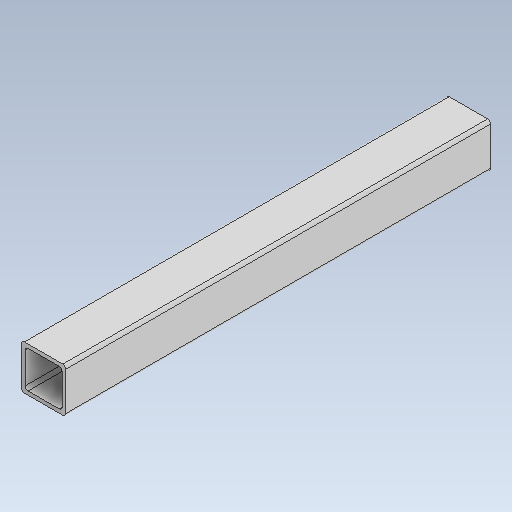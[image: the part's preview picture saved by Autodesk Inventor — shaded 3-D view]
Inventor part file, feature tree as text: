
AUTODESK INVENTOR PART (.ipt)
format: ipt  version: 2021 (Build 250183000, 183)  size: 134,656 bytes
history: native  units: mm
features: extrude x2, fillet x2, sketch x2
ambient origin geometry x8: Origin, YZ Plane, XZ Plane, XY Plane, X Axis, Y Axis, Z Axis, Center Point
bodies: Solid1 (feature_tree)
feature tree (6):
  extrude  "Extrusion1"  Depth=30.0mm
  fillet  "Fillet1"  Radius=30.0mm
  extrude  "Extrusion2"  Depth=30.0mm TaperAngle=0.0deg
  fillet  "Fillet2"  Radius=2.0mm
  sketch  "Sketch1"  dims[d0=287.5mm d1=143.75mm d2=30.0mm]
  sketch  "Sketch2"  dims[d3=15.0mm d4=30.0mm d5=0.0mm d6=2.0mm d7=2.5mm d8=2.5mm d9=2.5mm d10=2.5mm d11=300.0mm d12=0.0mm d13=2.0mm]
